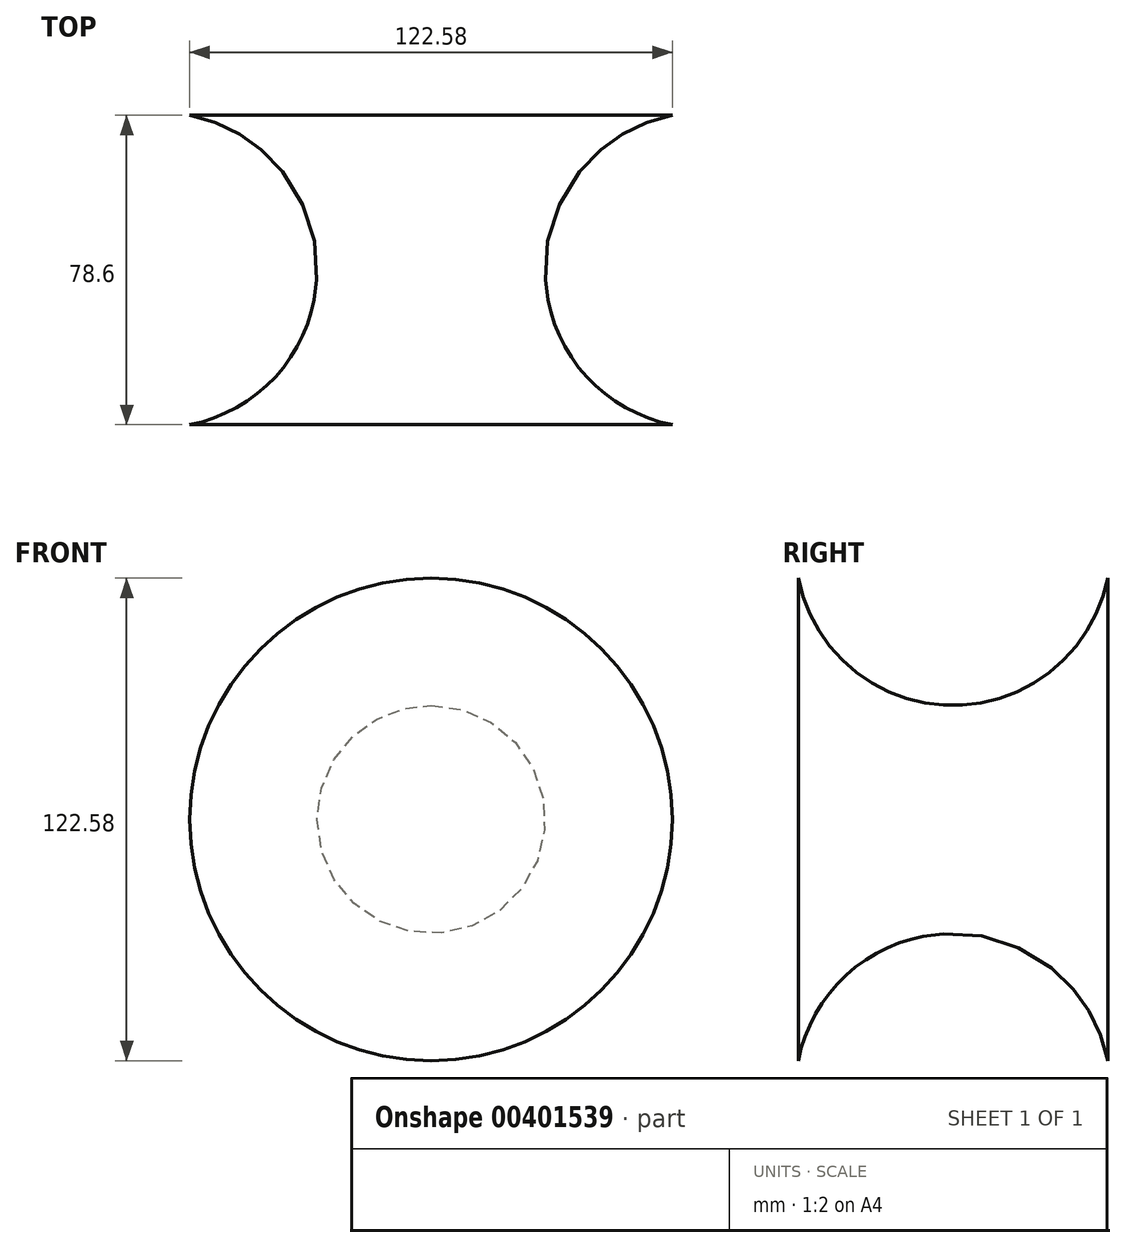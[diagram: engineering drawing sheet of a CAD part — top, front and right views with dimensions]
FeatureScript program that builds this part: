
annotation { "Feature Type Name" : "Feature", "Feature Type Description" : "" }
export const myFeature = defineFeature(function(context is Context, id is Id, definition is map)
    precondition{}
    {
        {
            var Q0;
            Q0=qCreatedBy(makeId("Top.planeOp"),FACE);
            var sketch = newSketch(context, id + "F0", { "sketchPlane" : qUnion([Q0])});
            skLineSegment(sketch, "E0", {"start": v(0, 32.32) * mm, "end": v(0, -46.28) * mm});
            skLineSegment(sketch, "E1", {"start": v(0, 32.32) * mm, "end": v(61.29, 32.32) * mm});
            skLineSegment(sketch, "E2", {"start": v(0, -46.28) * mm, "end": v(61.29, -46.28) * mm});
            skArc(sketch, "E3", {"start": v(61.29, 32.32) * mm, "mid": v(28.96, -6.98) * mm, "end": v(61.29, -46.28) * mm});
            skSolve(sketch);
        }
        {
            var Q0;
            Q0 = qSketchRegion(id + "F0", true);
            var Q1;
            Q1=sQuery(id+"F0.wireOp",EDGE,"E0");
            revolve(context, id + "F1", {"entities" : qUnion([Q0]), "axis" : qUnion([Q1]), "revolveType" : RevolveType.FULL});
        }
    });
